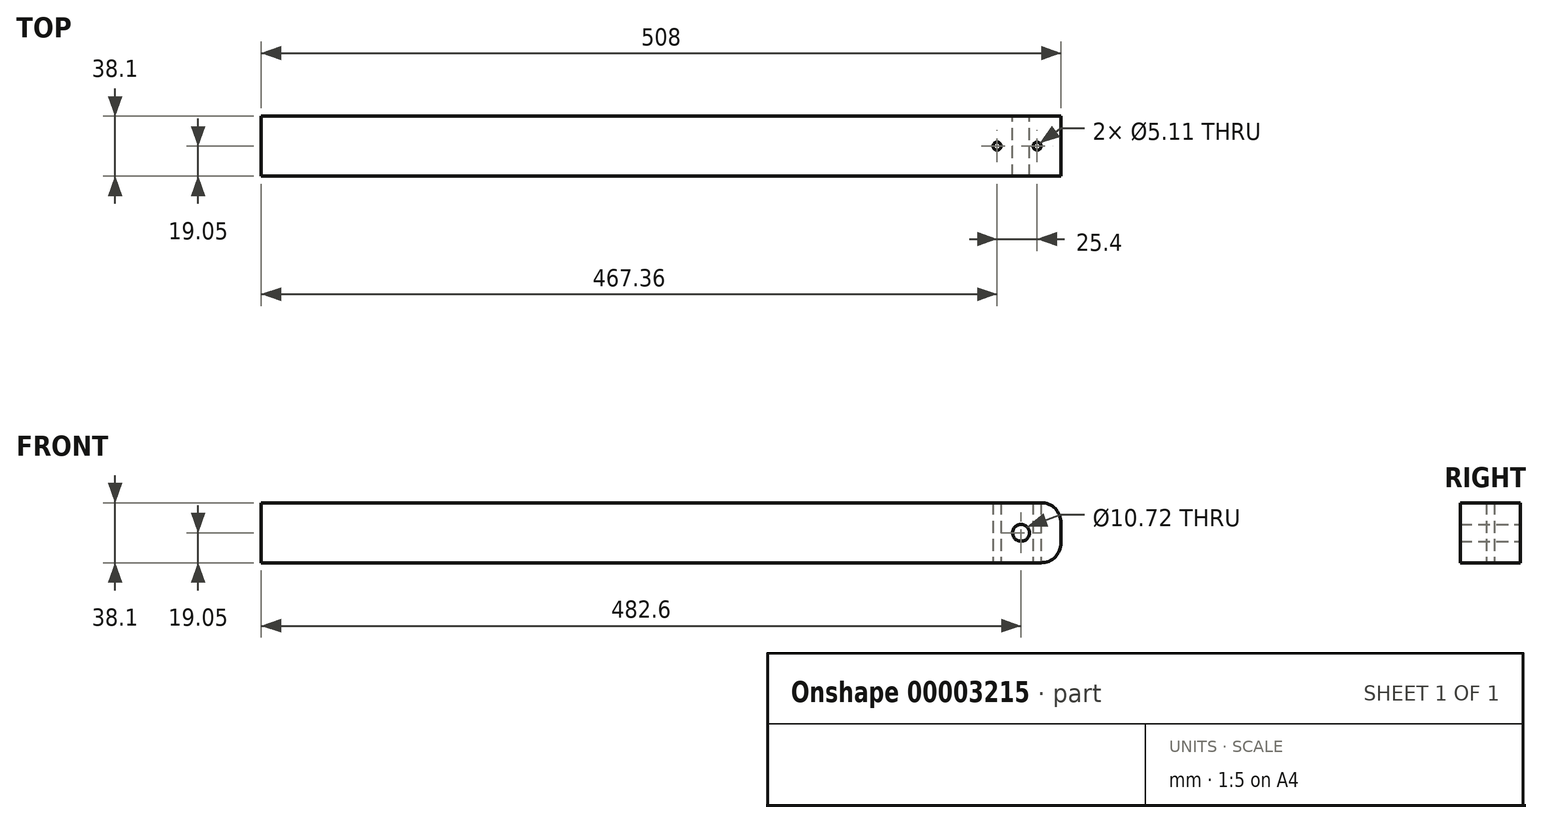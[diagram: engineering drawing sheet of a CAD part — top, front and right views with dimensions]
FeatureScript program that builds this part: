
annotation { "Feature Type Name" : "Feature", "Feature Type Description" : "" }
export const myFeature = defineFeature(function(context is Context, id is Id, definition is map)
    precondition{}
    {
        {
            var Q0;
            Q0=qCreatedBy(makeId("Front.planeOp"),FACE);
            var sketch = newSketch(context, id + "F0", { "sketchPlane" : qUnion([Q0])});
            skLineSegment(sketch, "E0", {"start": v(0, 0) * mm, "end": v(0, -38.1) * mm});
            skLineSegment(sketch, "E1", {"start": v(0, -38.1) * mm, "end": v(508, -38.1) * mm});
            skLineSegment(sketch, "E2", {"start": v(508, -38.1) * mm, "end": v(508, 0) * mm});
            skLineSegment(sketch, "E3", {"start": v(508, 0) * mm, "end": v(0, 0) * mm});
            skLineSegment(sketch, "E4", {"start": v(508, -19.05) * mm, "end": v(298.47, -19.05) * mm, "construction": true});
            skLineSegment(sketch, "E5", {"start": v(482.6, 0) * mm, "end": v(482.6, -38.1) * mm, "construction": true});
            skCircle(sketch, "E6", {"center": v(482.6, -19.05) * mm, "radius": 5.36 * mm});
            skSolve(sketch);
        }
        {
            var Q0;
            Q0=makeQuery(id+"F0.imprint","IMPRINT",FACE,{"disambiguationData":[TD([[makeQuery(id+"F0.imprint","IMPRINT",EDGE,{"derivedFrom":sQuery(id+"F0.wireOp",EDGE,"E0")}),1.0]])]});
            extrude(context, id + "F1", {"entities" : qUnion([Q0]), "endBound" : BoundingType.SYMMETRIC, "depth" : 38.1 * mm});
        }
        {
            var Q0;
            Q0=makeQuery(id+"F1.opExtrude","SWEPT_FACE",FACE,{"disambiguationData":[OSD([sQuery(id+"F0.wireOp",EDGE,"E1")])]});
            var sketch = newSketch(context, id + "F2", { "sketchPlane" : qUnion([Q0])});
            skLineSegment(sketch, "E7", {"start": v(508, 0) * mm, "end": v(369.1, 0) * mm, "construction": true});
            skLineSegment(sketch, "E8", {"start": v(492.76, 19.05) * mm, "end": v(492.76, -19.05) * mm, "construction": true});
            skLineSegment(sketch, "E9", {"start": v(467.36, 19.05) * mm, "end": v(467.36, -19.05) * mm, "construction": true});
            skCircle(sketch, "E10", {"center": v(492.76, 0) * mm, "radius": 2.55 * mm});
            skCircle(sketch, "E11", {"center": v(467.36, 0) * mm, "radius": 2.55 * mm});
            skSolve(sketch);
        }
        {
            var Q0;
            Q0 = qSketchRegion(id + "F2", true);
            extrude(context, id + "F3", {"entities" : qUnion([Q0]), "operationType" : NewBodyOperationType.REMOVE, "endBound" : BoundingType.THROUGH_ALL, "oppositeDirection" : true, "depth" : 25.4 * mm});
        }
        {
            var Q0;
            Q0=makeQuery(id+"F1.opExtrude","SWEPT_EDGE",EDGE,{"disambiguationData":[OSD([sQuery(id+"F0.wireOp",EDGE,"E2"),sQuery(id+"F0.wireOp",EDGE,"E3")])]});
            var Q1;
            Q1=makeQuery(id+"F1.opExtrude","SWEPT_EDGE",EDGE,{"disambiguationData":[OSD([sQuery(id+"F0.wireOp",EDGE,"E1"),sQuery(id+"F0.wireOp",EDGE,"E2")])]});
            fillet(context, id + "F4", {"entities" : qUnion([Q0, Q1]), "radius" : 12.7 * mm, "tangentPropagation" : true, "allowEdgeOverflow" : false});
        }
    });
